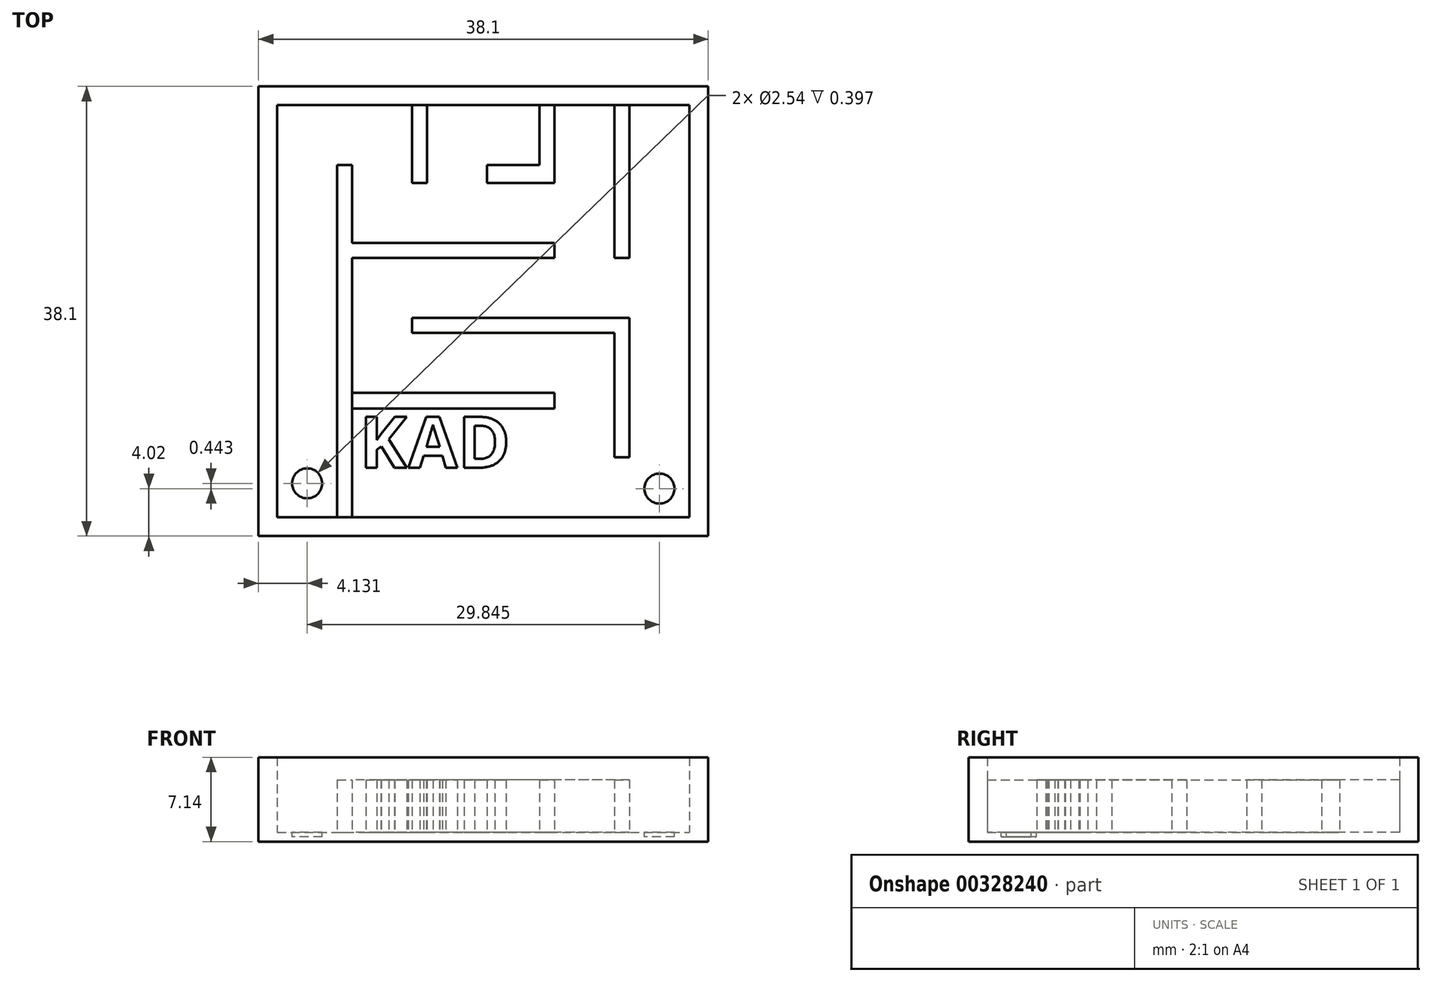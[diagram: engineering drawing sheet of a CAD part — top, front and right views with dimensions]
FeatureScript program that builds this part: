
annotation { "Feature Type Name" : "Feature", "Feature Type Description" : "" }
export const myFeature = defineFeature(function(context is Context, id is Id, definition is map)
    precondition{}
    {
        {
            var Q0;
            Q0=qCreatedBy(makeId("Top.planeOp"),FACE);
            var sketch = newSketch(context, id + "F0", { "sketchPlane" : qUnion([Q0])});
            skLineSegment(sketch, "E0.bottom", {"start": v(-26.47, 21.18) * mm, "end": v(11.63, 21.18) * mm});
            skLineSegment(sketch, "E0.top", {"start": v(-26.47, -16.92) * mm, "end": v(11.63, -16.92) * mm});
            skLineSegment(sketch, "E0.left", {"start": v(-26.47, 21.18) * mm, "end": v(-26.47, -16.92) * mm});
            skLineSegment(sketch, "E0.right", {"start": v(11.63, 21.18) * mm, "end": v(11.63, -16.92) * mm});
            skSolve(sketch);
        }
        {
            var Q0;
            Q0=makeQuery(id+"F0.imprint","IMPRINT",FACE,{"disambiguationData":[TD([[makeQuery(id+"F0.imprint","IMPRINT",EDGE,{"derivedFrom":sQuery(id+"F0.wireOp",EDGE,"E0.bottom")}),-1.0]])]});
            extrude(context, id + "F1", {"entities" : qUnion([Q0]), "depth" : 0.8 * mm});
        }
        {
            var Q0;
            Q0=makeQuery(id+"F1.opExtrude","CAP_FACE",FACE,{"disambiguationData":[OSD([sQuery(id+"F0.wireOp",EDGE,"E0.bottom"),sQuery(id+"F0.wireOp",EDGE,"E0.top"),sQuery(id+"F0.wireOp",EDGE,"E0.left"),sQuery(id+"F0.wireOp",EDGE,"E0.right")])],"isStart":false});
            var sketch = newSketch(context, id + "F2", { "sketchPlane" : qUnion([Q0])});
            skLineSegment(sketch, "E1.0", {"start": v(-24.88, 19.6) * mm, "end": v(10.05, 19.6) * mm});
            skLineSegment(sketch, "E2.0", {"start": v(10.05, 19.6) * mm, "end": v(10.05, -15.33) * mm});
            skLineSegment(sketch, "E3.0", {"start": v(-24.88, 19.6) * mm, "end": v(-24.88, -15.33) * mm});
            skLineSegment(sketch, "E4.0", {"start": v(-24.88, -15.33) * mm, "end": v(10.05, -15.33) * mm});
            skSolve(sketch);
        }
        {
            var Q0;
            Q0=makeQuery(id+"F2.imprint","IMPRINT",FACE,{"disambiguationData":[TD([[makeQuery(id+"F2.imprint","IMPRINT",EDGE,{"derivedFrom":sQuery(id+"F2.wireOp",EDGE,"E1.0")}),1.0]])]});
            extrude(context, id + "F3", {"entities" : qUnion([Q0]), "operationType" : NewBodyOperationType.ADD, "depth" : 6.35 * mm});
        }
        {
            var Q0;
            Q0=makeQuery(id+"F1.opExtrude","CAP_FACE",FACE,{"disambiguationData":[OSD([sQuery(id+"F0.wireOp",EDGE,"E0.bottom"),sQuery(id+"F0.wireOp",EDGE,"E0.top"),sQuery(id+"F0.wireOp",EDGE,"E0.left"),sQuery(id+"F0.wireOp",EDGE,"E0.right")])],"isStart":false});
            var sketch = newSketch(context, id + "F4", { "sketchPlane" : qUnion([Q0])});
            skLineSegment(sketch, "E5.bottom", {"start": v(-19.8, -15.33) * mm, "end": v(-18.53, -15.33) * mm});
            skLineSegment(sketch, "E5.top", {"start": v(-19.8, 14.51) * mm, "end": v(-18.53, 14.51) * mm});
            skLineSegment(sketch, "E5.left", {"start": v(-19.8, -15.33) * mm, "end": v(-19.8, 14.51) * mm});
            skLineSegment(sketch, "E5.right", {"start": v(-18.53, -15.33) * mm, "end": v(-18.53, 6.65) * mm});
            skLineSegment(sketch, "E6.bottom", {"start": v(-13.45, 19.6) * mm, "end": v(-12.18, 19.6) * mm});
            skLineSegment(sketch, "E6.top", {"start": v(-13.45, 13) * mm, "end": v(-12.18, 13) * mm});
            skLineSegment(sketch, "E6.left", {"start": v(-13.45, 19.6) * mm, "end": v(-13.45, 13) * mm});
            skLineSegment(sketch, "E6.right", {"start": v(-12.18, 19.6) * mm, "end": v(-12.18, 13) * mm});
            skLineSegment(sketch, "E7.bottom", {"start": v(-18.53, 7.92) * mm, "end": v(-1.38, 7.92) * mm});
            skLineSegment(sketch, "E7.top", {"start": v(-18.53, 6.65) * mm, "end": v(-1.38, 6.65) * mm});
            skLineSegment(sketch, "E7.right", {"start": v(-1.38, 7.92) * mm, "end": v(-1.38, 6.65) * mm});
            skLineSegment(sketch, "E8.bottom", {"start": v(4.97, 19.6) * mm, "end": v(3.7, 19.6) * mm});
            skLineSegment(sketch, "E8.top", {"start": v(4.97, 6.65) * mm, "end": v(3.7, 6.65) * mm});
            skLineSegment(sketch, "E8.left", {"start": v(4.97, 19.6) * mm, "end": v(4.97, 6.65) * mm});
            skLineSegment(sketch, "E8.right", {"start": v(3.7, 19.6) * mm, "end": v(3.7, 6.65) * mm});
            skLineSegment(sketch, "E9.bottom", {"start": v(4.97, 1.57) * mm, "end": v(-13.45, 1.57) * mm});
            skLineSegment(sketch, "E9.right", {"start": v(-13.45, 1.57) * mm, "end": v(-13.45, 0.3) * mm});
            skLineSegment(sketch, "E10.bottom", {"start": v(-18.53, -4.78) * mm, "end": v(-1.38, -4.78) * mm});
            skLineSegment(sketch, "E10.right", {"start": v(-1.38, -4.78) * mm, "end": v(-1.38, -6.1) * mm});
            skLineSegment(sketch, "E11.right", {"start": v(3.7, 0.3) * mm, "end": v(3.7, -10.25) * mm});
            skLineSegment(sketch, "E12.bottom", {"start": v(-2.65, 19.6) * mm, "end": v(-1.38, 19.6) * mm});
            skLineSegment(sketch, "E12.top", {"start": v(-2.65, 13) * mm, "end": v(-1.38, 13) * mm});
            skLineSegment(sketch, "E12.left", {"start": v(-2.65, 19.6) * mm, "end": v(-2.65, 14.51) * mm});
            skLineSegment(sketch, "E12.right", {"start": v(-1.38, 19.6) * mm, "end": v(-1.38, 14.51) * mm});
            skLineSegment(sketch, "E13.left", {"start": v(3.7, 14.51) * mm, "end": v(3.7, 13) * mm});
            skLineSegment(sketch, "E13.right", {"start": v(-7.1, 14.51) * mm, "end": v(-7.1, 13) * mm});
            skLineSegment(sketch, "E14.trimOffspring", {"start": v(-2.65, 13) * mm, "end": v(-2.65, 13) * mm});
            skLineSegment(sketch, "E15.trimOffspring", {"start": v(-1.38, 13) * mm, "end": v(-1.38, 13) * mm});
            skLineSegment(sketch, "E16.trimOffspring", {"start": v(-2.65, 14.51) * mm, "end": v(-7.1, 14.51) * mm});
            skLineSegment(sketch, "E17.trimOffspring", {"start": v(-2.65, 13) * mm, "end": v(-7.1, 13) * mm});
            skLineSegment(sketch, "E18.trimOffspring", {"start": v(3.7, 0.3) * mm, "end": v(-13.45, 0.3) * mm});
            skText(sketch, "E19", { "text": "KAD", "fontName": "OpenSans-Bold.ttf"});
            skLineSegment(sketch, "E20.trimOffspring", {"start": v(-18.53, 7.92) * mm, "end": v(-18.53, 14.51) * mm});
            skLineSegment(sketch, "E21", {"start": v(4.97, 1.57) * mm, "end": v(4.97, -10.25) * mm});
            skLineSegment(sketch, "E22", {"start": v(4.97, -10.25) * mm, "end": v(3.7, -10.25) * mm});
            skLineSegment(sketch, "E23", {"start": v(-24.88, -15.33) * mm, "end": v(-19.8, -15.33) * mm});
            skCircle(sketch, "E24", {"center": v(-22.34, -12.46) * mm, "radius": 1.27 * mm});
            skPoint(sketch, "E24.centerSnap0", {"position": v(-22.34, -15.33) * mm});
            skLineSegment(sketch, "E25", {"start": v(4.97, -15.33) * mm, "end": v(10.05, -15.33) * mm});
            skCircle(sketch, "E26", {"center": v(7.5, -12.9) * mm, "radius": 1.27 * mm});
            skPoint(sketch, "E26.centerSnap0", {"position": v(7.5, -15.33) * mm});
            skLineSegment(sketch, "E27", {"start": v(-1.38, 14.51) * mm, "end": v(-1.38, 13) * mm});
            skLineSegment(sketch, "E28", {"start": v(-1.38, -6.1) * mm, "end": v(-18.53, -6.1) * mm});
            const initialGuessF4  = {"E19": [-0.01791, -0.01114, 1, 0, 0.00435]};
            skSetInitialGuess(sketch, initialGuessF4);
            skSolve(sketch);
        }
        {
            var Q0;
            {var subQ1=sQuery(id+"F4.wireOp",EDGE,"E5.bottom");Q0=makeQuery(id+"F4.imprint","IMPRINT",FACE,{"disambiguationData":[TD([[makeQuery(id+"F4.imprint","IMPRINT",EDGE,{"derivedFrom":subQ1}),1.0]])]});}
            var Q1;
            Q1=makeQuery(id+"F4.imprint","IMPRINT",FACE,{"disambiguationData":[TD([[makeQuery(id+"F4.imprint","IMPRINT",EDGE,{"derivedFrom":sQuery(id+"F4.wireOp",EDGE,"E6.bottom")}),-1.0]])]});
            var Q2;
            Q2=makeQuery(id+"F4.imprint","IMPRINT",FACE,{"disambiguationData":[TD([[makeQuery(id+"F4.imprint","IMPRINT",EDGE,{"derivedFrom":sQuery(id+"F4.wireOp",EDGE,"E9.bottom")}),1.0]])]});
            var Q3;
            {var subQ1=sQuery(id+"F4.wireOp",EDGE,"E8.bottom");Q3=makeQuery(id+"F4.imprint","IMPRINT",FACE,{"disambiguationData":[TD([[makeQuery(id+"F4.imprint","IMPRINT",EDGE,{"derivedFrom":subQ1}),-1.0]])]});}
            var Q4;
            Q4=makeQuery(id+"F4.imprint","IMPRINT",FACE,{"disambiguationData":[TD([[makeQuery(id+"F4.imprint","IMPRINT",EDGE,{"derivedFrom":sQuery(id+"F4.wireOp",EDGE,"E12.bottom")}),-1.0]])]});
            extrude(context, id + "F5", {"entities" : qUnion([Q0, Q1, Q2, Q3, Q4]), "depth" : 4.44 * mm});
        }
        {
            var Q0;
            Q0=makeQuery(id+"F4.imprint","IMPRINT",FACE,{"disambiguationData":[TD([[makeQuery(id+"F4.imprint","IMPRINT",EDGE,{"derivedFrom":sQuery(id+"F4.wireOp",EDGE,"E26")}),1.0]])]});
            var Q1;
            Q1=makeQuery(id+"F4.imprint","IMPRINT",FACE,{"disambiguationData":[TD([[makeQuery(id+"F4.imprint","IMPRINT",EDGE,{"derivedFrom":sQuery(id+"F4.wireOp",EDGE,"E24")}),1.0]])]});
            extrude(context, id + "F6", {"entities" : qUnion([Q0, Q1]), "operationType" : NewBodyOperationType.REMOVE, "oppositeDirection" : true, "depth" : 0.4 * mm});
        }
        {
            var Q0;
            Q0=makeQuery(id+"F4.imprint","IMPRINT",FACE,{"disambiguationData":[TD([[makeQuery(id+"F4.imprint","IMPRINT",EDGE,{"derivedFrom":sQuery(id+"F4.wireOp",EDGE,"E19.sketch_text.stroke-0")}),-1.0]])]});
            var Q1;
            Q1=makeQuery(id+"F4.imprint","IMPRINT",FACE,{"disambiguationData":[TD([[makeQuery(id+"F4.imprint","IMPRINT",EDGE,{"derivedFrom":sQuery(id+"F4.wireOp",EDGE,"E19.sketch_text.stroke-13")}),-1.0]])]});
            var Q2;
            Q2=makeQuery(id+"F4.imprint","IMPRINT",FACE,{"disambiguationData":[TD([[makeQuery(id+"F4.imprint","IMPRINT",EDGE,{"derivedFrom":sQuery(id+"F4.wireOp",EDGE,"E19.sketch_text.stroke-25")}),-1.0]])]});
            extrude(context, id + "F7", {"entities" : qUnion([Q0, Q1, Q2]), "depth" : 4.44 * mm});
        }
        {
            var Q0;
            {var subQ0=sQuery(id+"F4.wireOp",EDGE,"E10.bottom");Q0=makeQuery(id+"F4.imprint","IMPRINT",FACE,{"disambiguationData":[TD([[makeQuery(id+"F4.imprint","IMPRINT",EDGE,{"derivedFrom":subQ0}),-1.0]])]});}
            extrude(context, id + "F8", {"entities" : qUnion([Q0]), "depth" : 4.44 * mm});
        }
    });
